# Revit family: 2620483 - P2 Pot Sink Centre 2400mm
name_source: partatom
category: Plumbing Fixtures
revit_build: Autodesk Revit 2018 (Build: 20170927_1515(x64)
units: mm (PartAtom-declared; Revit-internal decimal feet)

## family parameters
Always vertical = Yes
Cut with Voids When Loaded = No
OmniClass Number = 23.40.70.17
OmniClass Title = Industrial and Manufacturing Equipment and Furnishings
Part Type = Normal
Room Calculation Point = No
Round Connector Dimension = Use Diameter
Shared = No
Work Plane-Based = No

## types (1)
- P2 Pot Sink Centre
    Assembly Code = E1090300
    Bowl Size = 600mm x 500mm x 300mm
    CW Connection = No
    Dimensions = 2400mm x 650mm x 1050mm
    HW Connection = No
    Manufacturer = Franke South Africa (Pty) Ltd
    Material = Grade 304 18/10
    Model = P2 Pot Sink, 2400mm Long
    Product Code = 2620483
    Vent Connection = No
    Waste Connection = Yes

## geometry (parser evidence)
native form markers: Blend x10, Sweep x2
no freeform markers — native parametric forms only
